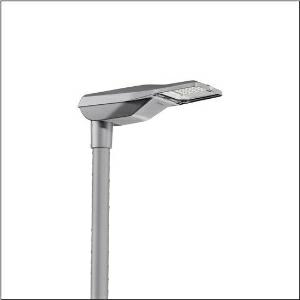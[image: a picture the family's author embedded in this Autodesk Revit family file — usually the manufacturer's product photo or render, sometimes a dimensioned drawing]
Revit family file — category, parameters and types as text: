
# Revit family: streetlight_sl_21_iq_micro___stw1_0a_5xe1e31g08db_041b
name_source: partatom
category: Lighting Fixtures
units: mm (PartAtom-declared; Revit-internal decimal feet)

## family parameters
Cut with Voids When Loaded = No
Host = Face
Light Source = No
Part Type = Normal
Room Calculation Point = No
Round Connector Dimension = Use Diameter
Shared = No

## types (1)
- --- (1 x LED, 4810 lm, 36.4 W, 3000K)
    Apparent Load = 36 VA
    CIE Flux Codes = 38 75 98 100 100
    Color Rendering = 70
    Color Temperature = 3000K
    Default Elevation = 1800 mm
    Description = Streetlight SL 21 iQ micro, mast luminaire, primary light control with lens, of PMMA, primary optical cover: cover, of toughened safety glass, transparent, light distribution: STW1.0a, light emission: direct distribution, primary light characteristic: asymmetric, installation type: post-top, side-entry, LED, High Power LED, rated luminous flux: 4.810lm, luminous efficacy: 132lm/W, light colour: 730, colour temperature: 3000K, control gear: iQ Street-Remote, control: Street-Remote, Auto-Match, Temp-Guard, Lumen-Switch, Night-Set, Smart-Wire, Light-Fading, Desk-Remote (wireless, voltage-free reading and setting of iQ features in the workshop via application-optimized NFC function/RFID function), optimised constant luminous flux control (CLO 2.0), pre-setting: linear dimming characteristic, mains connection: 220..240V, AC, 50/60Hz, start of lifetime: 36W, end of service life: 38W, reduction: 16W, luminaire housing, of diecast aluminium, powder-coated, Siteco® metallic grey (DB 702S), corrosivity category C5 mid according to DIN EN ISO 12944, please order mast flange separately, inclination adjustable: 0°, 5°, 10°, 15°, sealing non-destructively replaceable, multi-level sealing system, length: 528mm, width: 235mm, height: 110mm, mast flange for spigot size: 42mm (side-entry): 5XC10008XM4, 60/48mm (side-entry/post-top): 5XC10108XM2, 76/60mm (side-entry/post-top): 5XC10108XM1, protection rating (complete): IP66, insulation class (complete): insulation class II (safety insulation), certification: CE, ENEC, ENEC+, VDE, impact resistance: IK10, permissible operating ambient temperature for outdoor applications: -40..+50°C, standard-compliant lighting for roads and squares, packaging unit: 1 piece

Light Distribution: STW1.0a
    Height = 110 mm
    Lamp = 1 x LED
    Lamp Light Flux = 4810 lm
    Lamp Power = 36.4 W
    Lamp count = 1
    Length = 528 mm
    Luminous efficacy = 132 lm/W
    Manufacturer = Siteco
    ModVariant = No
    Model = 5XE1E31G08DB
    Number of Poles = 1
    OnlyDefault = Yes
    Power Factor = 1
    Product Name = Streetlight SL 21 iQ micro | STW1.0a
    Product group = mast luminaire | pylon top
    ProductGroupID = 6100
    Protection Class = Protection class II
    Protection Degree = IP 66
    RLX_Detail_Level = 1
    RLX_Emergency_Light_Flux = 0 lm
    RLX_Emergency_Type = 0
    RLX_Emergency_Type_DB = No
    RlxData = <blob elided: 99289 chars, md5=5b588c2c>
    Socket = socket
    Standby Power = 0 W
    System Light Flux = 4810 lm
    System Power = 36 W
    Type Comments = factory setting: luminous flux: 100 % | dim-lin: 254 | 715 mA
    Type Image = l_1006881.jpg
    URL = http://relux.com
    VarID = @adj_155500
    Voltage = 0 V
    Weight = 0.00 kg
    Width = 235 mm

## geometry (parser evidence)
native form markers: Blend x4, Sweep x9
no freeform markers — native parametric forms only
